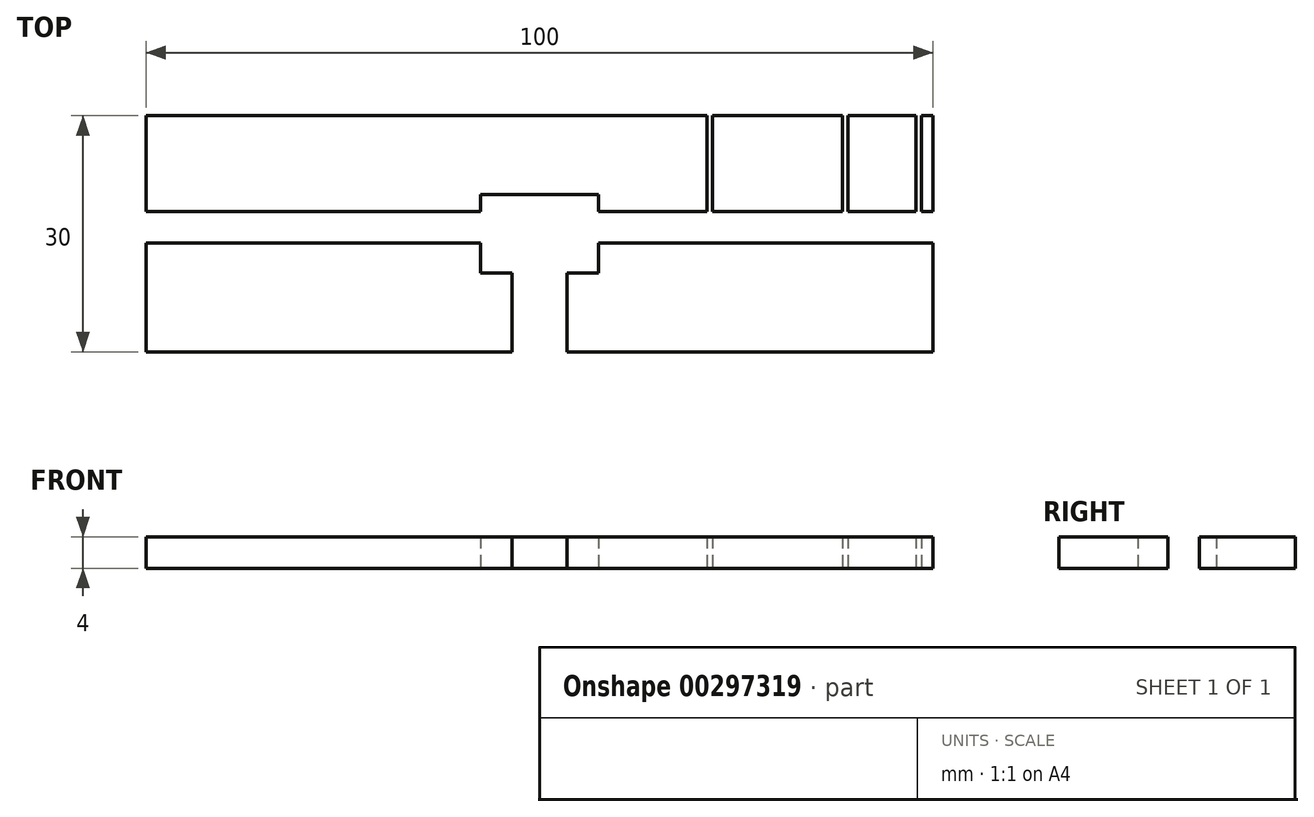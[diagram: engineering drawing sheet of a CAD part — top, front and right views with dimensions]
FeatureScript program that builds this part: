
annotation { "Feature Type Name" : "Feature", "Feature Type Description" : "" }
export const myFeature = defineFeature(function(context is Context, id is Id, definition is map)
    precondition{}
    {
        {
            var Q0;
            Q0=qCreatedBy(makeId("Top.planeOp"),FACE);
            var sketch = newSketch(context, id + "F0", { "sketchPlane" : qUnion([Q0])});
            skLineSegment(sketch, "E0.bottom", {"start": v(50, -15) * mm, "end": v(-50, -15) * mm});
            skLineSegment(sketch, "E0.top", {"start": v(50, 15) * mm, "end": v(-50, 15) * mm});
            skLineSegment(sketch, "E0.left", {"start": v(50, -15) * mm, "end": v(50, 15) * mm});
            skLineSegment(sketch, "E0.right", {"start": v(-50, -15) * mm, "end": v(-50, 15) * mm});
            skPoint(sketch, "E0.middle", {"position": v(0, 0) * mm});
            skSolve(sketch);
        }
        {
            var Q0;
            Q0=qCreatedBy(makeId("Top.planeOp"),FACE);
            var sketch = newSketch(context, id + "F1", { "sketchPlane" : qUnion([Q0])});
            skPoint(sketch, "E1.middle", {"position": v(0, 0) * mm});
            skLineSegment(sketch, "E2.bottom", {"start": v(7.5, -5) * mm, "end": v(-7.5, -5) * mm});
            skLineSegment(sketch, "E2.top", {"start": v(7.5, 5) * mm, "end": v(-7.5, 5) * mm});
            skLineSegment(sketch, "E2.left", {"start": v(7.5, -5) * mm, "end": v(7.5, 5) * mm});
            skLineSegment(sketch, "E2.right", {"start": v(-7.5, -5) * mm, "end": v(-7.5, 5) * mm});
            skLineSegment(sketch, "E3.bottom", {"start": v(-3.5, -5) * mm, "end": v(3.5, -5) * mm});
            skLineSegment(sketch, "E3.top", {"start": v(-3.5, -20) * mm, "end": v(3.5, -20) * mm});
            skLineSegment(sketch, "E3.left", {"start": v(-3.5, -5) * mm, "end": v(-3.5, -20) * mm});
            skLineSegment(sketch, "E3.right", {"start": v(3.5, -5) * mm, "end": v(3.5, -20) * mm});
            skLineSegment(sketch, "E4.bottom", {"start": v(-50, -1.2) * mm, "end": v(50, -1.2) * mm});
            skLineSegment(sketch, "E4.top", {"start": v(-50, 2.8) * mm, "end": v(50, 2.8) * mm});
            skLineSegment(sketch, "E4.left", {"start": v(-50, -1.2) * mm, "end": v(-50, 2.8) * mm});
            skLineSegment(sketch, "E4.right", {"start": v(50, -1.2) * mm, "end": v(50, 2.8) * mm});
            skLineSegment(sketch, "E5.bottom", {"start": v(21.3, 2.8) * mm, "end": v(22, 2.8) * mm});
            skLineSegment(sketch, "E5.top", {"start": v(21.3, 31.79) * mm, "end": v(22, 31.79) * mm});
            skLineSegment(sketch, "E5.left", {"start": v(21.3, 2.8) * mm, "end": v(21.3, 31.79) * mm});
            skLineSegment(sketch, "E5.right", {"start": v(22, 2.8) * mm, "end": v(22, 31.79) * mm});
            skLineSegment(sketch, "E6.bottom", {"start": v(47.8, 2.8) * mm, "end": v(48.5, 2.8) * mm});
            skLineSegment(sketch, "E6.top", {"start": v(47.8, 38.42) * mm, "end": v(48.5, 38.42) * mm});
            skLineSegment(sketch, "E6.left", {"start": v(47.8, 2.8) * mm, "end": v(47.8, 38.42) * mm});
            skLineSegment(sketch, "E6.right", {"start": v(48.5, 2.8) * mm, "end": v(48.5, 38.42) * mm});
            skLineSegment(sketch, "E7.bottom", {"start": v(38.47, 2.8) * mm, "end": v(39.17, 2.8) * mm});
            skLineSegment(sketch, "E7.top", {"start": v(38.47, 25.3) * mm, "end": v(39.17, 25.3) * mm});
            skLineSegment(sketch, "E7.left", {"start": v(38.47, 2.8) * mm, "end": v(38.47, 25.3) * mm});
            skLineSegment(sketch, "E7.right", {"start": v(39.17, 2.8) * mm, "end": v(39.17, 25.3) * mm});
            skSolve(sketch);
        }
        {
            var Q0;
            Q0 = qSketchRegion(id + "F0", true);
            extrude(context, id + "F2", {"entities" : qUnion([Q0]), "depth" : 4 * mm});
        }
        {
            var Q0;
            Q0 = qSketchRegion(id + "F1", true);
            extrude(context, id + "F3", {"entities" : qUnion([Q0]), "operationType" : NewBodyOperationType.REMOVE, "depth" : 4 * mm});
        }
    });
